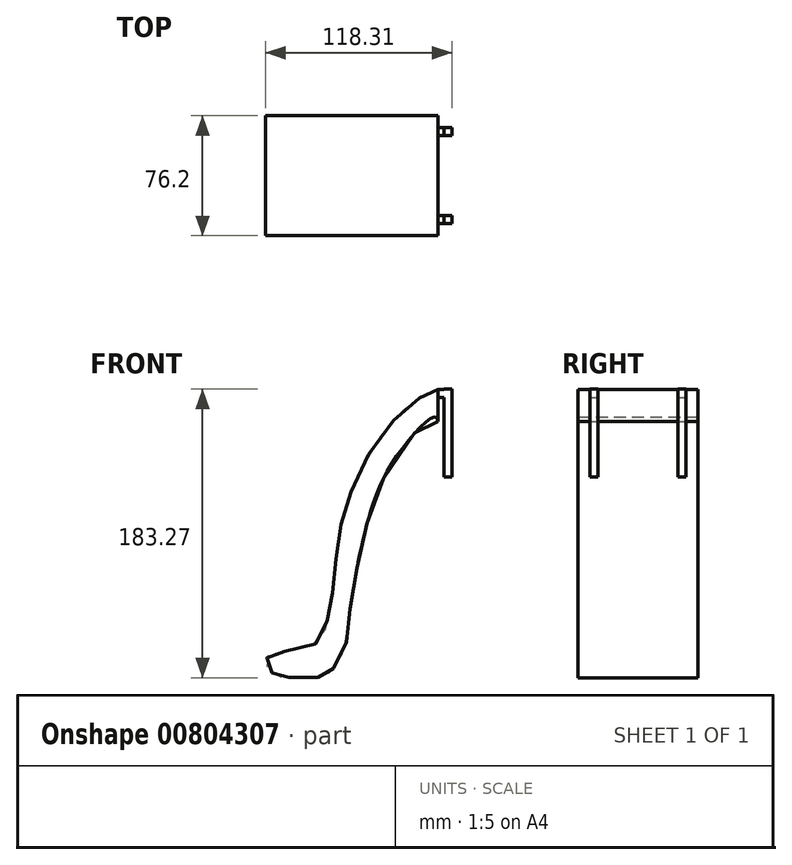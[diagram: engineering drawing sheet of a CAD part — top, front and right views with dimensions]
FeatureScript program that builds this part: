
annotation { "Feature Type Name" : "Feature", "Feature Type Description" : "" }
export const myFeature = defineFeature(function(context is Context, id is Id, definition is map)
    precondition{}
    {
        {
            var Q0;
            Q0=qCreatedBy(makeId("Front.planeOp"),FACE);
            var sketch = newSketch(context, id + "F0", { "sketchPlane" : qUnion([Q0])});
            skFitSpline(sketch, "E0", {"points": [v(0, 182.97) * mm, v(-9.32, 179.54) * mm, v(-32.23, 158.92) * mm, v(-54.8, 118.92) * mm, v(-63.14, 89.13) * mm, v(-66.7, 56.97) * mm, v(-70.6, 34.8) * mm, v(-79.18, 20.62) * mm, v(-104.18, 15.77) * mm, v(-108.6, 12.65) * mm, v(-108.62, 6.13) * mm, v(-99.13, 0.3) * mm, v(-94.14, 0.29) * mm, v(-89.76, 0.3) * mm, v(-83.97, 0.3) * mm, v(-76.94, 0.27) * mm, v(-73.14, 0.27) * mm, v(-61.04, 13.8) * mm, v(-56.47, 38.63) * mm, v(-48.26, 84.46) * mm, v(-24.52, 143.15) * mm, v(0, 162.7) * mm], "startDerivative": vector(-361.15, -23.3) * mm, "endDerivative": vector(0, -434.72) * mm});
            skLineSegment(sketch, "E1", {"start": v(0, 182.97) * mm, "end": v(0, 162.7) * mm});
            skSolve(sketch);
        }
        {
            var Q0;
            Q0 = qSketchRegion(id + "F0", true);
            extrude(context, id + "F1", {"entities" : qUnion([Q0]), "depth" : 76.2 * mm, "offsetDistance" : 25.4 * mm});
        }
        {
            var Q0;
            Q0=qCreatedBy(makeId("Right.planeOp"),FACE);
            var sketch = newSketch(context, id + "F2", { "sketchPlane" : qUnion([Q0])});
            skLineSegment(sketch, "E2", {"start": v(-12.7, 182.97) * mm, "end": v(-7.62, 182.97) * mm});
            skLineSegment(sketch, "E3.left", {"start": v(-68.58, 182.97) * mm, "end": v(-68.58, 179.87) * mm});
            skLineSegment(sketch, "E3.right", {"start": v(-63.5, 182.97) * mm, "end": v(-63.5, 179.87) * mm});
            skLineSegment(sketch, "E4.top", {"start": v(-12.7, 177.9) * mm, "end": v(-7.62, 177.9) * mm});
            skLineSegment(sketch, "E4.left", {"start": v(-12.7, 182.97) * mm, "end": v(-12.7, 177.9) * mm});
            skLineSegment(sketch, "E4.right", {"start": v(-7.62, 182.97) * mm, "end": v(-7.62, 177.9) * mm});
            skLineSegment(sketch, "E5.bottom", {"start": v(-68.58, 182.97) * mm, "end": v(-63.5, 182.97) * mm});
            skLineSegment(sketch, "E5.top", {"start": v(-68.58, 177.9) * mm, "end": v(-63.5, 177.9) * mm});
            skLineSegment(sketch, "E5.left", {"start": v(-68.58, 182.97) * mm, "end": v(-68.58, 177.9) * mm});
            skLineSegment(sketch, "E5.right", {"start": v(-63.5, 182.97) * mm, "end": v(-63.5, 177.9) * mm});
            skSolve(sketch);
        }
        {
            var Q0;
            Q0=makeQuery(id+"F2.imprint","IMPRINT",FACE,{"disambiguationData":[TD([[makeQuery(id+"F2.imprint","IMPRINT",EDGE,{"derivedFrom":sQuery(id+"F2.wireOp",EDGE,"E2")}),-1.0]])]});
            var Q1;
            {var subQ0=sQuery(id+"F2.wireOp",EDGE,"E5.bottom");Q1=makeQuery(id+"F2.imprint","IMPRINT",FACE,{"disambiguationData":[TD([[makeQuery(id+"F2.imprint","IMPRINT",EDGE,{"derivedFrom":subQ0}),-1.0]])]});}
            extrude(context, id + "F3", {"entities" : qUnion([Q0, Q1]), "operationType" : NewBodyOperationType.ADD, "depth" : 3.8 * mm, "offsetDistance" : 25.4 * mm});
        }
        {
            var Q0;
            Q0=qCreatedBy(makeId("Top.planeOp"),FACE);
            var sketch = newSketch(context, id + "F4", { "sketchPlane" : qUnion([Q0])});
            skLineSegment(sketch, "E6.bottom", {"start": v(3.81, -7.62) * mm, "end": v(8.9, -7.62) * mm});
            skLineSegment(sketch, "E6.top", {"start": v(3.81, -12.7) * mm, "end": v(8.9, -12.7) * mm});
            skLineSegment(sketch, "E6.left", {"start": v(3.81, -7.62) * mm, "end": v(3.81, -12.7) * mm});
            skLineSegment(sketch, "E6.right", {"start": v(8.9, -7.62) * mm, "end": v(8.9, -12.7) * mm});
            skLineSegment(sketch, "E7.bottom", {"start": v(3.81, -63.5) * mm, "end": v(8.9, -63.5) * mm});
            skLineSegment(sketch, "E7.top", {"start": v(3.81, -68.58) * mm, "end": v(8.9, -68.58) * mm});
            skLineSegment(sketch, "E7.left", {"start": v(3.81, -63.5) * mm, "end": v(3.81, -68.58) * mm});
            skLineSegment(sketch, "E7.right", {"start": v(8.9, -63.5) * mm, "end": v(8.9, -68.58) * mm});
            skSolve(sketch);
        }
        {
            var Q0;
            Q0=makeQuery(id+"F4.imprint","IMPRINT",FACE,{"disambiguationData":[TD([[makeQuery(id+"F4.imprint","IMPRINT",EDGE,{"derivedFrom":sQuery(id+"F4.wireOp",EDGE,"E6.bottom")}),-1.0]])]});
            var Q1;
            Q1=makeQuery(id+"F4.imprint","IMPRINT",FACE,{"disambiguationData":[TD([[makeQuery(id+"F4.imprint","IMPRINT",EDGE,{"derivedFrom":sQuery(id+"F4.wireOp",EDGE,"E7.bottom")}),-1.0]])]});
            extrude(context, id + "F5", {"entities" : qUnion([Q0, Q1]), "operationType" : NewBodyOperationType.ADD, "depth" : 183.24 * mm, "offsetDistance" : 25.4 * mm});
        }
        {
            var Q0;
            Q0=qCreatedBy(makeId("Top.planeOp"),FACE);
            var sketch = newSketch(context, id + "F6", { "sketchPlane" : qUnion([Q0])});
            skLineSegment(sketch, "E8.bottom", {"start": v(3.81, -12.7) * mm, "end": v(8.88, -12.7) * mm});
            skLineSegment(sketch, "E8.top", {"start": v(3.81, -7.62) * mm, "end": v(8.88, -7.62) * mm});
            skLineSegment(sketch, "E8.left", {"start": v(3.81, -12.7) * mm, "end": v(3.81, -7.62) * mm});
            skLineSegment(sketch, "E8.right", {"start": v(8.88, -12.7) * mm, "end": v(8.88, -7.62) * mm});
            skLineSegment(sketch, "E9.bottom", {"start": v(3.81, -63.5) * mm, "end": v(8.9, -63.5) * mm});
            skLineSegment(sketch, "E9.top", {"start": v(3.81, -68.58) * mm, "end": v(8.9, -68.58) * mm});
            skLineSegment(sketch, "E9.left", {"start": v(3.81, -63.5) * mm, "end": v(3.81, -68.58) * mm});
            skLineSegment(sketch, "E9.right", {"start": v(8.9, -63.5) * mm, "end": v(8.9, -68.58) * mm});
            skSolve(sketch);
        }
        {
            var Q0;
            Q0 = qSketchRegion(id + "F6", true);
            extrude(context, id + "F7", {"entities" : qUnion([Q0]), "operationType" : NewBodyOperationType.REMOVE, "depth" : 127.36 * mm, "offsetDistance" : 25.4 * mm});
        }
    });
